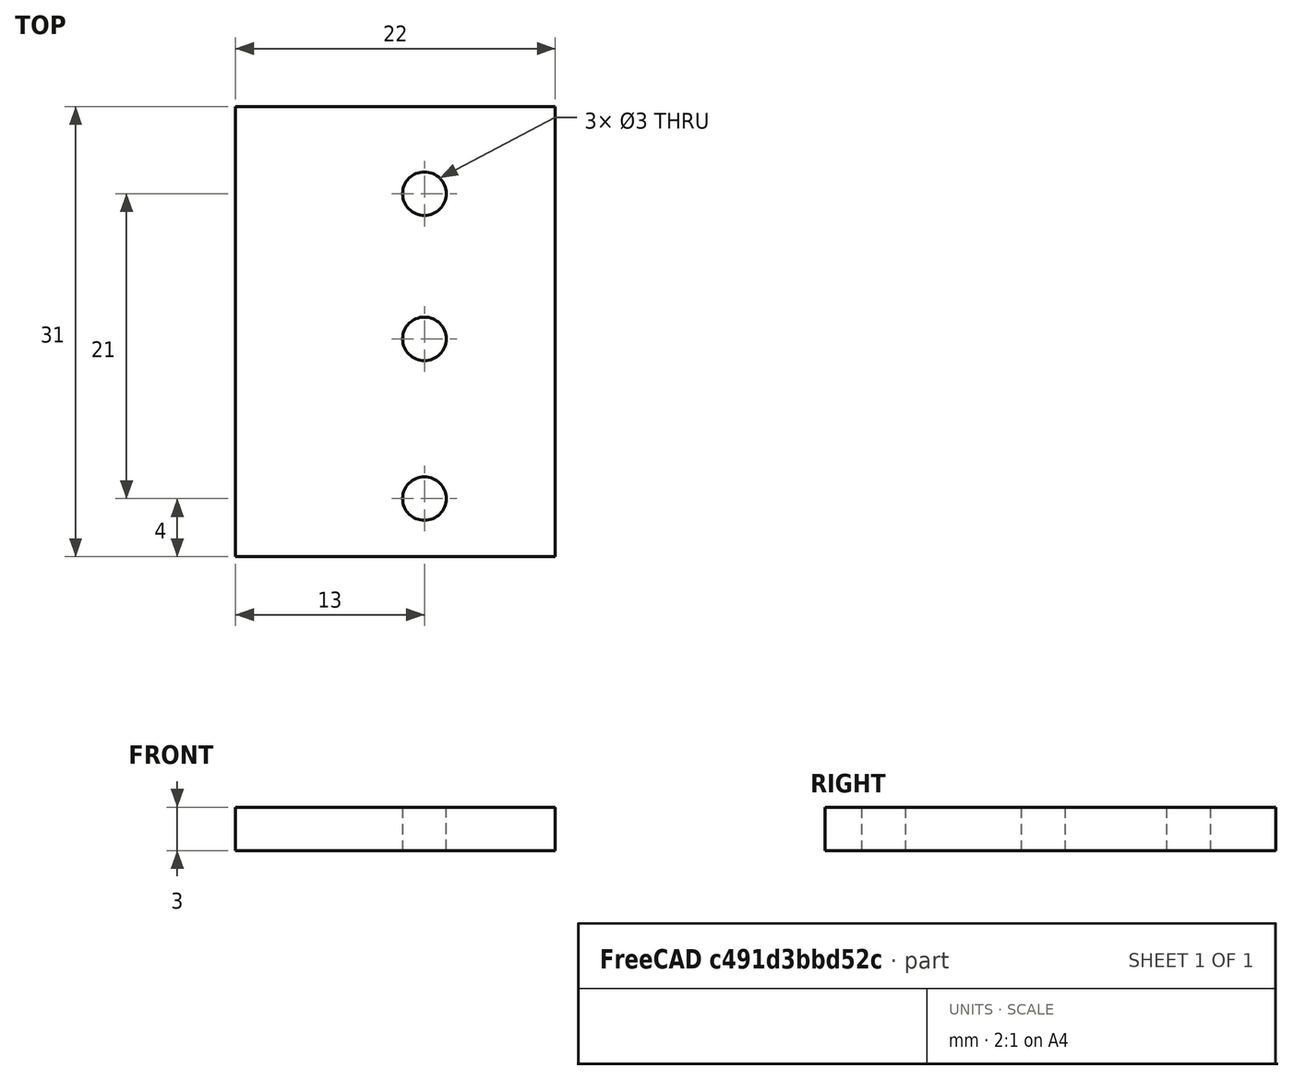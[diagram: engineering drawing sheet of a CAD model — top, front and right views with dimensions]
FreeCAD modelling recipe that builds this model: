
FCSTD DOCUMENT  (FreeCAD 0.19R24276 (Git))
Label: Endpoint_1_support
License: All rights reserved
LicenseURL: http://en.wikipedia.org/wiki/All_rights_reserved
objects: Sketcher::SketchObject×1, PartDesign::Pad×1, PartDesign::Body×1
note: 4 computed .brp shape members not serialized (recipe doc carries the construction recipe); baked Part::Feature solids carry a one-line shape summary decoded from their .brp

FEATURE [Sketcher::SketchObject] Sketch
  FullyConstrained = true
  MapMode = 5
  Support = -> [XY_Plane]
  sketch-geometry (10):
    g0: LineSegment StartX=0 StartY=0 StartZ=0 EndX=22 EndY=0 EndZ=0
    g1: LineSegment StartX=22 StartY=0 StartZ=0 EndX=22 EndY=31 EndZ=0
    g2: LineSegment StartX=22 StartY=31 StartZ=0 EndX=0 EndY=31 EndZ=0
    g3: LineSegment StartX=0 StartY=31 StartZ=0 EndX=0 EndY=0 EndZ=0
    g4: LineSegment StartX=0 StartY=25 StartZ=0 EndX=22 EndY=25 EndZ=0
    g5: LineSegment StartX=0 StartY=15 StartZ=0 EndX=22 EndY=15 EndZ=0
    g6: LineSegment StartX=0 StartY=4 StartZ=0 EndX=22 EndY=4 EndZ=0
    g7: Circle CenterX=13 CenterY=25 CenterZ=0 NormalX=0 NormalY=0 NormalZ=1 AngleXU=0 Radius=1.5
    g8: Circle CenterX=13 CenterY=4 CenterZ=0 NormalX=0 NormalY=0 NormalZ=1 AngleXU=0 Radius=1.5
    g9: Circle CenterX=13 CenterY=15 CenterZ=0 NormalX=0 NormalY=0 NormalZ=1 AngleXU=0 Radius=1.5
  constraints (32):
    c: Coincident(g0,g1)
    c: Coincident(g1,g2)
    c: Coincident(g2,g3)
    c: Coincident(g3,g0)
    c: Horizontal(g0)
    c: Horizontal(g2)
    c: Vertical(g1)
    c: Vertical(g3)
    c: Coincident(g0,g-1)
    c: Horizontal(g4)
    c: Horizontal(g5)
    c: Horizontal(g6)
    c: PointOnObject(g5,g3)
    c: PointOnObject(g4,g3)
    c: PointOnObject(g6,g3)
    c: PointOnObject(g6,g1)
    c: PointOnObject(g5,g1)
    c: PointOnObject(g4,g1)
    c: DistanceY(g6,g5) = 11
    c: DistanceY(g5,g4) = 10
    c: DistanceY(g0,g6) = 4
    c: DistanceY(g4,g2) = 6
    c: DistanceX(g0,g0) = 22
    c: PointOnObject(g7,g4)
    c: PointOnObject(g9,g5)
    c: DistanceX(g7,g4) = 9
    c: DistanceX(g9,g5) = 9
    c: PointOnObject(g8,g6)
    c: DistanceX(g8,g6) = 9
    c: Diameter(g7) = 3
    c: Equal(g7,g9)
    c: Equal(g7,g8)
FEATURE [PartDesign::Pad] Pad
  Direction = (1,1,1)
  Length = 3
  Length2 = 100
  Profile = -> Sketch
  Type = 0
FEATURE [PartDesign::Body] Body
  Group = -> [Sketch,Pad]
  Origin = -> Origin
  Tip = -> Pad
